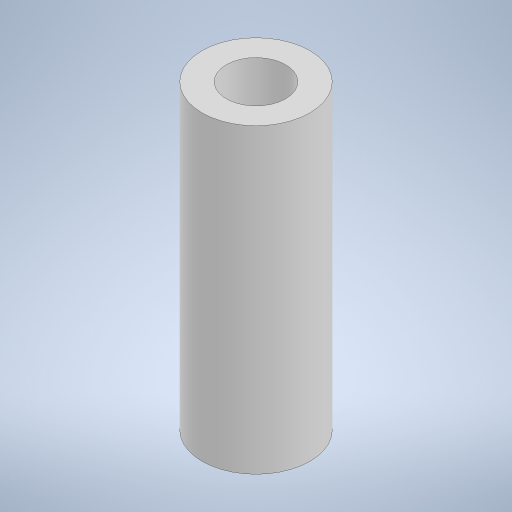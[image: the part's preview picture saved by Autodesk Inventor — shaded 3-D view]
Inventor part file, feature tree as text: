
AUTODESK INVENTOR PART (.ipt)
format: ipt  version: 2023 (Build 270158000, 158)  size: 211,456 bytes
history: native  units: mm
features: other x1, extrude x1, sketch x1
ambient origin geometry x8: Origin, YZ Plane, XZ Plane, XY Plane, X Axis, Y Axis, Z Axis, Center Point
bodies: Body1 (feature_tree)
feature tree (3):
  other  "ソリッド1"
  extrude  "押し出し1"  Depth=2.2mm
  sketch  "スケッチ1"
